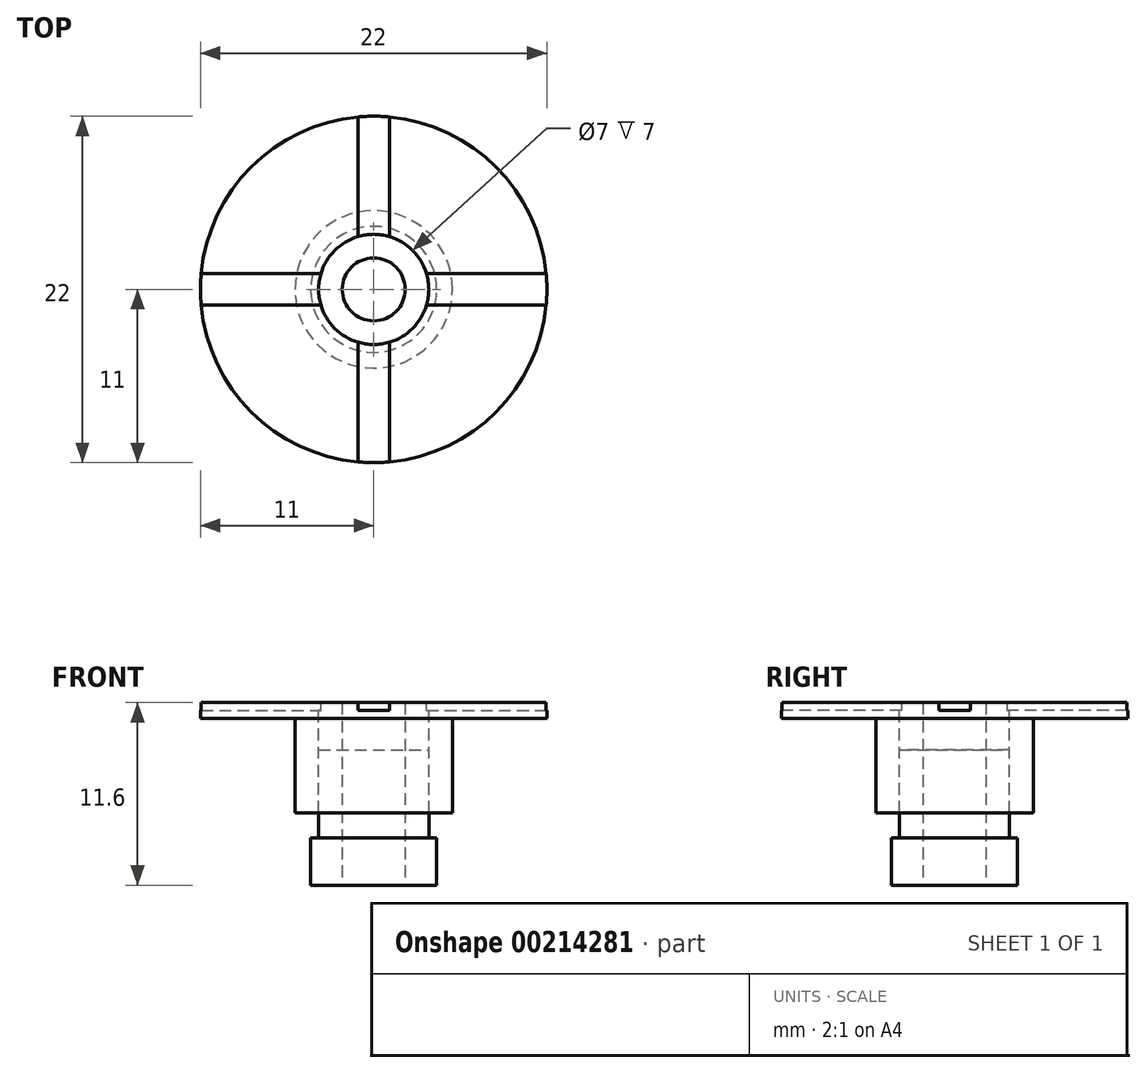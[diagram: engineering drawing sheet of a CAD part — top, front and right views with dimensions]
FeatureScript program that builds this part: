
annotation { "Feature Type Name" : "Feature", "Feature Type Description" : "" }
export const myFeature = defineFeature(function(context is Context, id is Id, definition is map)
    precondition{}
    {
        {
            var Q0;
            Q0=qCreatedBy(makeId("Top.planeOp"),FACE);
            var sketch = newSketch(context, id + "F0", { "sketchPlane" : qUnion([Q0])});
            skCircle(sketch, "E0", {"center": v(0, 0) * mm, "radius": 11 * mm});
            skSolve(sketch);
        }
        {
            var Q0;
            Q0 = qSketchRegion(id + "F0", true);
            extrude(context, id + "F1", {"entities" : qUnion([Q0]), "depth" : 1 * mm});
        }
        {
            var Q0;
            Q0=makeQuery(id+"F1.opExtrude","CAP_FACE",FACE,{"disambiguationData":[OSD([sQuery(id+"F0.wireOp",EDGE,"E0")])],"isStart":true});
            var sketch = newSketch(context, id + "F2", { "sketchPlane" : qUnion([Q0])});
            skCircle(sketch, "E1", {"center": v(0, 0) * mm, "radius": 5 * mm});
            skSolve(sketch);
        }
        {
            var Q0;
            Q0 = qSketchRegion(id + "F2", true);
            extrude(context, id + "F3", {"entities" : qUnion([Q0]), "operationType" : NewBodyOperationType.ADD, "depth" : 6 * mm});
        }
        {
            var Q0;
            Q0=makeQuery(id+"F1.opExtrude","CAP_FACE",FACE,{"disambiguationData":[OSD([sQuery(id+"F0.wireOp",EDGE,"E0")])],"isStart":false});
            var sketch = newSketch(context, id + "F4", { "sketchPlane" : qUnion([Q0])});
            skCircle(sketch, "E2", {"center": v(0, 0) * mm, "radius": 3.5 * mm});
            skSolve(sketch);
        }
        {
            var Q0;
            Q0 = qSketchRegion(id + "F4", true);
            extrude(context, id + "F5", {"entities" : qUnion([Q0]), "operationType" : NewBodyOperationType.REMOVE, "oppositeDirection" : true, "depth" : 11.6 * mm});
        }
        {
            var Q0;
            Q0=makeQuery(id+"F1.opExtrude","CAP_FACE",FACE,{"disambiguationData":[OSD([sQuery(id+"F0.wireOp",EDGE,"E0")])],"isStart":false});
            var sketch = newSketch(context, id + "F6", { "sketchPlane" : qUnion([Q0])});
            skArc(sketch, "E3", {"start": v(-10.95, 1) * mm, "mid": v(-11, 0) * mm, "end": v(-10.95, -1) * mm});
            skArc(sketch, "E4", {"start": v(-3.35, 1) * mm, "mid": v(-3.5, 0) * mm, "end": v(-3.35, -1) * mm});
            skLineSegment(sketch, "E5.bottom", {"start": v(-10.95, 1) * mm, "end": v(-3.35, 1) * mm});
            skLineSegment(sketch, "E5.top", {"start": v(-10.95, -1) * mm, "end": v(-3.35, -1) * mm});
            skLineSegment(sketch, "E5.left", {"start": v(-10.95, 1) * mm, "end": v(-10.95, -1) * mm});
            skLineSegment(sketch, "E5.right", {"start": v(10.95, 1) * mm, "end": v(10.95, -1) * mm});
            skLineSegment(sketch, "E6.bottom", {"start": v(-1, 10.95) * mm, "end": v(1, 10.95) * mm});
            skLineSegment(sketch, "E6.top", {"start": v(-1, -10.95) * mm, "end": v(1, -10.95) * mm});
            skLineSegment(sketch, "E6.left", {"start": v(-1, 10.95) * mm, "end": v(-1, 3.35) * mm});
            skLineSegment(sketch, "E6.right", {"start": v(1, 10.95) * mm, "end": v(1, 3.35) * mm});
            skArc(sketch, "E7.trimOffspring", {"start": v(1, 3.35) * mm, "mid": v(0, 3.5) * mm, "end": v(-1, 3.35) * mm});
            skArc(sketch, "E8.trimOffspring", {"start": v(3.35, -1) * mm, "mid": v(3.5, 0) * mm, "end": v(3.35, 1) * mm});
            skArc(sketch, "E9.trimOffspring", {"start": v(-1, -3.35) * mm, "mid": v(0, -3.5) * mm, "end": v(1, -3.35) * mm});
            skLineSegment(sketch, "E10.trimOffspring", {"start": v(3.35, 1) * mm, "end": v(10.95, 1) * mm});
            skLineSegment(sketch, "E11.trimOffspring", {"start": v(3.35, -1) * mm, "end": v(10.95, -1) * mm});
            skLineSegment(sketch, "E12.trimOffspring", {"start": v(1, -3.35) * mm, "end": v(1, -10.95) * mm});
            skLineSegment(sketch, "E13.trimOffspring", {"start": v(-1, -3.35) * mm, "end": v(-1, -10.95) * mm});
            skArc(sketch, "E14.trimOffspring", {"start": v(1, 10.95) * mm, "mid": v(0, 11) * mm, "end": v(-1, 10.95) * mm});
            skArc(sketch, "E15.trimOffspring", {"start": v(10.95, -1) * mm, "mid": v(11, 0) * mm, "end": v(10.95, 1) * mm});
            skArc(sketch, "E16.trimOffspring", {"start": v(-1, -10.95) * mm, "mid": v(0, -11) * mm, "end": v(1, -10.95) * mm});
            skSolve(sketch);
        }
        {
            var Q0;
            Q0 = qSketchRegion(id + "F6", true);
            extrude(context, id + "F7", {"entities" : qUnion([Q0]), "operationType" : NewBodyOperationType.REMOVE, "oppositeDirection" : true, "depth" : 0.5 * mm});
        }
        {
            var Q0;
            Q0=makeQuery(id+"F3.opExtrude","CAP_FACE",FACE,{"disambiguationData":[OSD([sQuery(id+"F2.wireOp",EDGE,"E1")])],"isStart":false});
            var sketch = newSketch(context, id + "F8", { "sketchPlane" : qUnion([Q0])});
            skCircle(sketch, "E17", {"center": v(0, 0) * mm, "radius": 3.5 * mm});
            skSolve(sketch);
        }
        {
            var Q0;
            Q0 = qSketchRegion(id + "F8", true);
            extrude(context, id + "F9", {"entities" : qUnion([Q0]), "depth" : (11.6 - 7 - 3) * mm, "hasSecondDirection" : true, "secondDirectionOppositeDirection" : true, "secondDirectionDepth" : 4 * mm});
        }
        {
            var Q0;
            Q0=makeQuery(id+"F9.opExtrude","CAP_FACE",FACE,{"disambiguationData":[OSD([sQuery(id+"F8.wireOp",EDGE,"E17")])],"isStart":false});
            var sketch = newSketch(context, id + "F10", { "sketchPlane" : qUnion([Q0])});
            skCircle(sketch, "E18", {"center": v(0, 0) * mm, "radius": 4 * mm});
            skSolve(sketch);
        }
        {
            var Q0;
            Q0 = qSketchRegion(id + "F10", true);
            extrude(context, id + "F11", {"entities" : qUnion([Q0]), "depth" : 3 * mm});
        }
        {
            var Q0;
            Q0=makeQuery(id+"F11.opExtrude","CAP_FACE",FACE,{"disambiguationData":[OSD([sQuery(id+"F10.wireOp",EDGE,"E18")])],"isStart":false});
            var sketch = newSketch(context, id + "F12", { "sketchPlane" : qUnion([Q0])});
            skCircle(sketch, "E19", {"center": v(0, 0) * mm, "radius": 2 * mm});
            skSolve(sketch);
        }
        {
            var Q0;
            Q0 = qSketchRegion(id + "F12", true);
            extrude(context, id + "F13", {"entities" : qUnion([Q0]), "oppositeDirection" : true, "depth" : 11.6 * mm});
        }
    });
